# Revit family: 1438xxx Astro Parallel
name_source: partatom
category: Lighting Fixtures
units: mm (PartAtom-declared; Revit-internal decimal feet)

## family parameters
Always vertical = Yes
Cut with Voids When Loaded = No
Host = Wall
Light Source = No
OmniClass Number = 23.80.70.00
OmniClass Title = Lighting
Part Type = Normal
Room Calculation Point = No
Round Connector Dimension = Use Diameter
Shared = No

## types (1)
- Astro 1438xxx Parallel
    ADA compliant = N / A
    Default Elevation = 0 mm  [stored 0 ft]
    Dimmable = Lamp Dependent
    Dimming Method = Lamp Dependent
    Driver Required = No
    Efficacy (lm/w) = Lamp Dependent
    Electrical Class = 2
    Lamp = E27
    Location / IP Rating = Indoor / IP20 / Zone 3
    Main Finish = Ceramic
    Main Material = Ceramic
    Manufacturer = Astro Lighting Ltd
    Manufacturer URL - Europe and Rest of World = www.astrolighting.com
    Manufacturer URL - North America = us.astrolighting.com
    Power (Watts) = 12W Max LED
    Product CCT = Lamp Dependent
    Product CRI = Lamp Dependent
    Product Dimensions (MM) = H 130 W 320 D 110mm
    Product Location = Wall
    Product Name = Parallel
    Product SKU = 1438001
    Product URL = https://www.astrolighting.com
    Product Weight (KG) = 0.4
    URL = www.astrolighting.com

note: [stored X ft] marks values corroborated as IEEE doubles in the binary element streams (Revit-internal decimal feet)

## geometry (parser evidence)
native form markers: Sweep x3
no freeform markers — native parametric forms only
